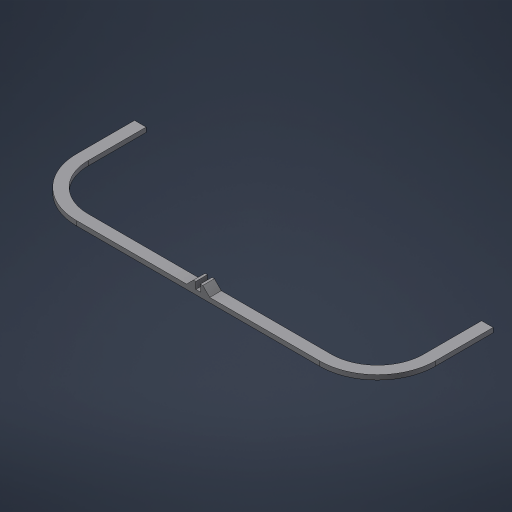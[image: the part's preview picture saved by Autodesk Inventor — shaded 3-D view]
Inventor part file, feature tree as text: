
AUTODESK INVENTOR PART (.ipt)
format: ipt  version: 2023.5 (Build 275446000, 446)  size: 440,320 bytes
history: native  units: mm
features: sketch x2, extrude x2, mirror x1, chamfer x1
ambient origin geometry x8: Origin, YZ Plane, XZ Plane, XY Plane, X Axis, Y Axis, Z Axis, Center Point
bodies: Volumenkörper1 (feature_tree)
feature tree (6):
  sketch  "Skizze1"  dims[d0=5.0mm d2=50.0mm]
  extrude  "Extrusion1"  Depth=50.0mm
  extrude  "Extrusion2"  Depth=150.0mm
  mirror  "Spiegeln1"
  chamfer  "Fase1"  Distance=10.0mm
  sketch  "Skizze2"  dims[d3=25.0mm d4=150.0mm d6=10.0mm d7=2.0mm d8=2.0mm d9=0.0mm d10=5.0mm d11=0.0mm d12=3.0mm d13=2.0mm d14=45.0deg d15=5.0mm d16=3.0mm d17=60.0mm d19=25.0mm]
